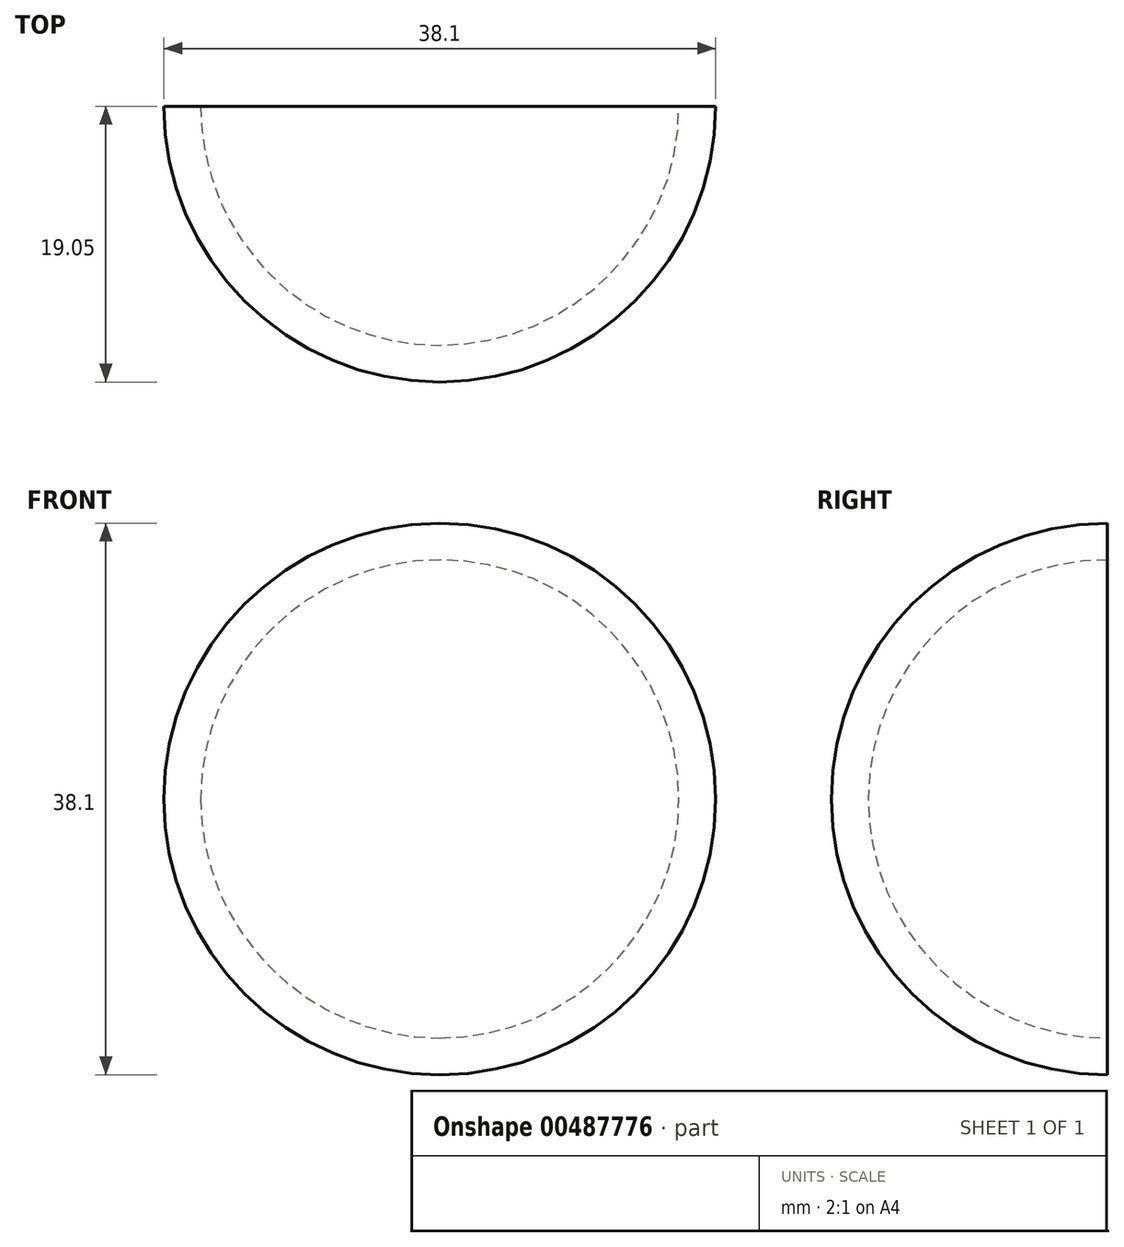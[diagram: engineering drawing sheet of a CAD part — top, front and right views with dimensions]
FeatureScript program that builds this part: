
annotation { "Feature Type Name" : "Feature", "Feature Type Description" : "" }
export const myFeature = defineFeature(function(context is Context, id is Id, definition is map)
    precondition{}
    {
        {
            var Q0;
            Q0=qCreatedBy(makeId("Front.planeOp"),FACE);
            var sketch = newSketch(context, id + "F0", { "sketchPlane" : qUnion([Q0])});
            skArc(sketch, "E0", {"start": v(0, -19.05) * mm, "mid": v(19.05, 0) * mm, "end": v(0, 19.05) * mm});
            skLineSegment(sketch, "E1", {"start": v(0, 0) * mm, "end": v(0, -19.05) * mm});
            skPoint(sketch, "E2.orphan", {"position": v(0, 19.05) * mm});
            skLineSegment(sketch, "E3", {"start": v(0, 19.05) * mm, "end": v(0, 0) * mm});
            skLineSegment(sketch, "E4", {"start": v(0, 0) * mm, "end": v(0, 60.73) * mm, "construction": true});
            skSolve(sketch);
        }
        {
            var Q0;
            Q0 = qSketchRegion(id + "F0", true);
            var Q1;
            Q1=sQuery(id+"F0.wireOp",EDGE,"E4");
            revolve(context, id + "F1", {"entities" : qUnion([Q0]), "axis" : qUnion([Q1]), "revolveType" : RevolveType.ONE_DIRECTION, "oppositeDirection" : true, "angle" : 180 * degree});
        }
        {
            var Q0;
            Q0=makeQuery(id+"F1.opRevolve","CAP_FACE",FACE,{"disambiguationData":[OSD([sQuery(id+"F0.wireOp",EDGE,"E0"),sQuery(id+"F0.wireOp",EDGE,"E1"),sQuery(id+"F0.wireOp",EDGE,"E3")])],"isStart":true});
            shell(context, id + "F2", {"entities" : qUnion([Q0]), "thickness" : 2.54 * mm});
        }
    });
